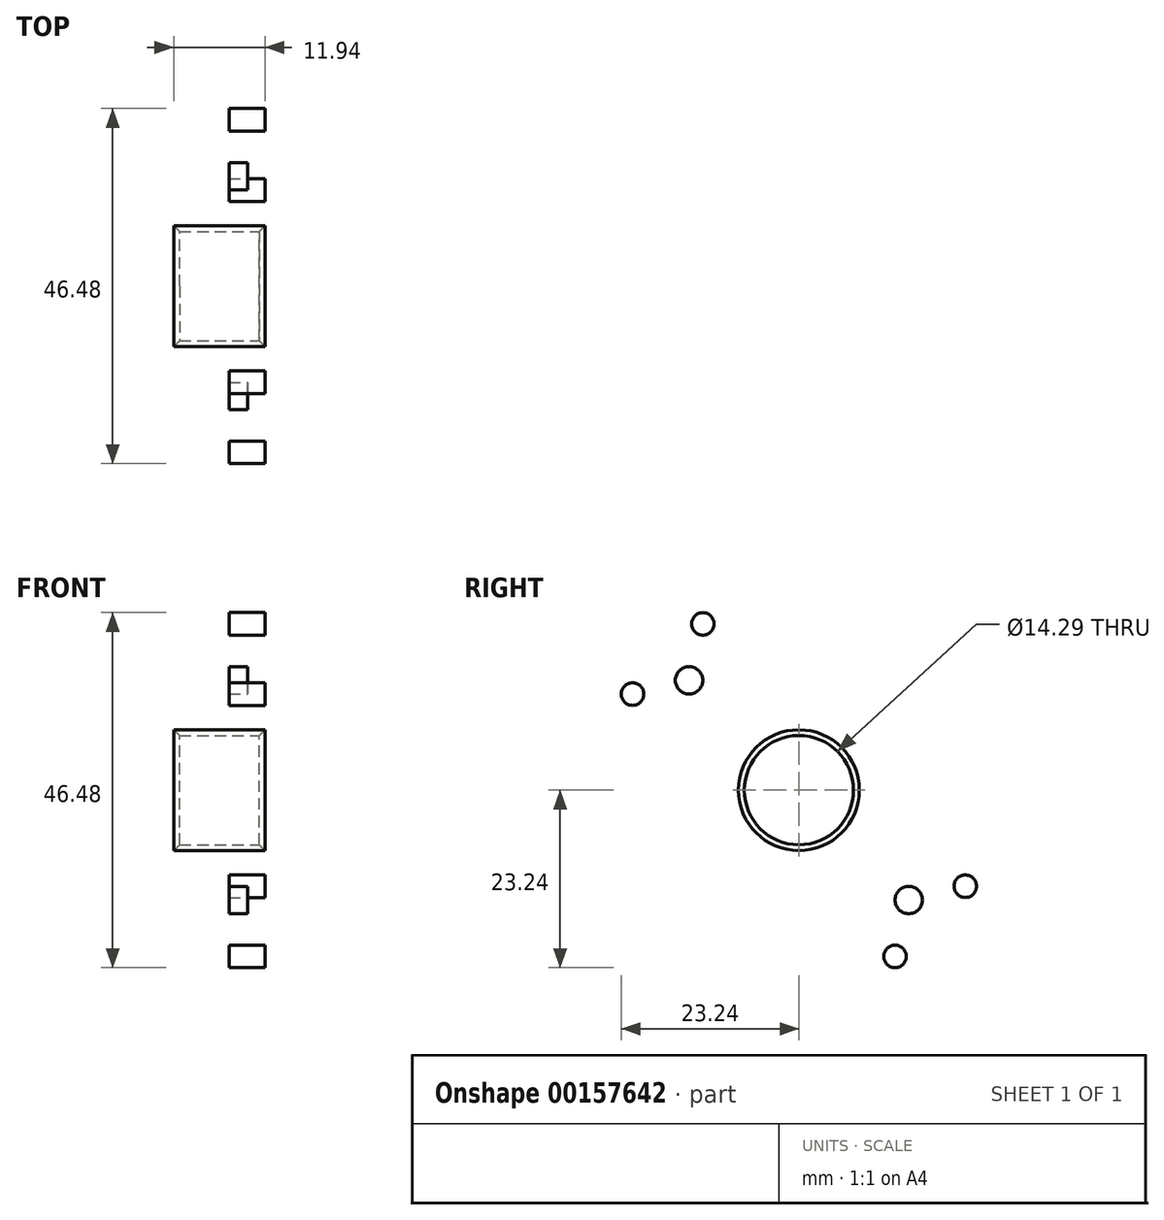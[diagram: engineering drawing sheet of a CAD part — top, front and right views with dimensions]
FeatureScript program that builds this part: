
annotation { "Feature Type Name" : "Feature", "Feature Type Description" : "" }
export const myFeature = defineFeature(function(context is Context, id is Id, definition is map)
    precondition{}
    {
        {
            var Q0;
            Q0=qCreatedBy(makeId("Right.planeOp"),FACE);
            var sketch = newSketch(context, id + "F0", { "sketchPlane" : qUnion([Q0])});
            skCircle(sketch, "E0", {"center": v(0, 0) * mm, "radius": 7.14 * mm});
            skCircle(sketch, "E1", {"center": v(0, 0) * mm, "radius": 11.94 * mm});
            skCircle(sketch, "E2", {"center": v(0, 0) * mm, "radius": 12.32 * mm});
            skCircle(sketch, "E3", {"center": v(0, 0) * mm, "radius": 17.02 * mm});
            skCircle(sketch, "E4", {"center": v(0, 0) * mm, "radius": 22.99 * mm});
            skCircle(sketch, "E5", {"center": v(0, 0) * mm, "radius": 27.3 * mm});
            skSolve(sketch);
        }
        {
            var Q0;
            Q0=makeQuery(id+"F0.imprint","IMPRINT",FACE,{"disambiguationData":[TD([[makeQuery(id+"F0.imprint","IMPRINT",EDGE,{"derivedFrom":sQuery(id+"F0.wireOp",EDGE,"E1")}),-1.0]])]});
            var Q1;
            Q1=makeQuery(id+"F0.imprint","IMPRINT",FACE,{"disambiguationData":[TD([[makeQuery(id+"F0.imprint","IMPRINT",EDGE,{"derivedFrom":sQuery(id+"F0.wireOp",EDGE,"E0")}),-1.0]])]});
            extrude(context, id + "F1", {"entities" : qUnion([Q0, Q1]), "oppositeDirection" : true, "depth" : 11.94 * mm});
        }
        {
            var Q0;
            Q0=makeQuery(id+"F0.imprint","IMPRINT",FACE,{"disambiguationData":[TD([[makeQuery(id+"F0.imprint","IMPRINT",EDGE,{"derivedFrom":sQuery(id+"F0.wireOp",EDGE,"E2")}),-1.0]])]});
            extrude(context, id + "F2", {"entities" : qUnion([Q0]), "operationType" : NewBodyOperationType.ADD, "oppositeDirection" : true, "depth" : 7.62 * mm});
        }
        {
            var Q0;
            Q0=makeQuery(id+"F0.imprint","IMPRINT",FACE,{"disambiguationData":[TD([[makeQuery(id+"F0.imprint","IMPRINT",EDGE,{"derivedFrom":sQuery(id+"F0.wireOp",EDGE,"E4")}),-1.0]])]});
            var Q1;
            Q1=makeQuery(id+"F0.imprint","IMPRINT",FACE,{"disambiguationData":[TD([[makeQuery(id+"F0.imprint","IMPRINT",EDGE,{"derivedFrom":sQuery(id+"F0.wireOp",EDGE,"E3")}),-1.0]])]});
            extrude(context, id + "F3", {"entities" : qUnion([Q0, Q1]), "operationType" : NewBodyOperationType.ADD, "oppositeDirection" : true, "depth" : 4.7 * mm});
        }
        {
            var Q0;
            Q0=makeQuery(id+"F1.opExtrude","CAP_EDGE",EDGE,{"disambiguationData":[OSD([sQuery(id+"F0.wireOp",EDGE,"E2")])],"isStart":false});
            chamfer(context, id + "F4", {"entities" : qUnion([Q0]), "width" : 1.52 * mm, "tangentPropagation" : true});
        }
        {
            var Q0;
            Q0=makeQuery(id+"F1.opExtrude","CAP_EDGE",EDGE,{"disambiguationData":[OSD([sQuery(id+"F0.wireOp",EDGE,"E0")])],"isStart":false});
            var Q1;
            Q1=makeQuery(id+"F1.opExtrude","CAP_EDGE",EDGE,{"disambiguationData":[OSD([sQuery(id+"F0.wireOp",EDGE,"E0")])],"isStart":true});
            chamfer(context, id + "F5", {"entities" : qUnion([Q0, Q1]), "width" : 0.76 * mm, "tangentPropagation" : true});
        }
        {
            var Q0;
            {var subQ0=sQuery(id+"F0.wireOp",EDGE,"E3");var subQ1=sQuery(id+"F0.wireOp",EDGE,"E2");Q0=makeQuery(id+"F3.boolean.opBoolean","MERGE",FACE,{"derivedFrom":[makeQuery(id+"F2.boolean.opBoolean","MERGE",FACE,{"derivedFrom":[makeQuery(id+"F1.opExtrude","CAP_FACE",FACE,{"disambiguationData":[OSD([sQuery(id+"F0.wireOp",EDGE,"E0"),subQ1])],"isStart":true}),makeQuery(id+"F2.opExtrude","CAP_FACE",FACE,{"disambiguationData":[OSD([subQ1,subQ0])],"isStart":true})]}),makeQuery(id+"F3.opExtrude","CAP_FACE",FACE,{"disambiguationData":[OSD([subQ0,sQuery(id+"F0.wireOp",EDGE,"E5")])],"isStart":true})]});}
            var sketch = newSketch(context, id + "F6", { "sketchPlane" : qUnion([Q0])});
            skCircle(sketch, "E6", {"center": v(12.57, 21.77) * mm, "radius": 1.47 * mm});
            skCircle(sketch, "E7", {"center": v(21.77, 12.57) * mm, "radius": 1.47 * mm});
            skCircle(sketch, "E8.MirrorC", {"center": v(-12.57, 21.77) * mm, "radius": 1.47 * mm});
            skCircle(sketch, "E9.MirrorC", {"center": v(-21.77, 12.57) * mm, "radius": 1.47 * mm});
            skCircle(sketch, "E10.MirrorC", {"center": v(-21.77, -12.57) * mm, "radius": 1.47 * mm});
            skCircle(sketch, "E11.MirrorC", {"center": v(-12.57, -21.77) * mm, "radius": 1.47 * mm});
            skCircle(sketch, "E12.MirrorC", {"center": v(12.57, -21.77) * mm, "radius": 1.47 * mm});
            skCircle(sketch, "E13.MirrorC", {"center": v(21.77, -12.57) * mm, "radius": 1.47 * mm});
            skCircle(sketch, "E14", {"center": v(14.38, 14.38) * mm, "radius": 1.8 * mm});
            skCircle(sketch, "E15.MirrorC", {"center": v(-14.38, 14.38) * mm, "radius": 1.8 * mm});
            skCircle(sketch, "E16.MirrorC", {"center": v(-14.38, -14.38) * mm, "radius": 1.8 * mm});
            skCircle(sketch, "E17.MirrorC", {"center": v(14.38, -14.38) * mm, "radius": 1.8 * mm});
            skSolve(sketch);
        }
        {
            var Q0;
            Q0=makeQuery(id+"F6.imprint","IMPRINT",FACE,{"disambiguationData":[TD([[makeQuery(id+"F6.imprint","IMPRINT",EDGE,{"derivedFrom":sQuery(id+"F6.wireOp",EDGE,"E8.MirrorC")}),-1.0]])]});
            var Q1;
            Q1=makeQuery(id+"F6.imprint","IMPRINT",FACE,{"disambiguationData":[TD([[makeQuery(id+"F6.imprint","IMPRINT",EDGE,{"derivedFrom":sQuery(id+"F6.wireOp",EDGE,"E9.MirrorC")}),-1.0]])]});
            var Q2;
            Q2=makeQuery(id+"F6.imprint","IMPRINT",FACE,{"disambiguationData":[TD([[makeQuery(id+"F6.imprint","IMPRINT",EDGE,{"derivedFrom":sQuery(id+"F6.wireOp",EDGE,"E10.MirrorC")}),1.0]])]});
            var Q3;
            Q3=makeQuery(id+"F6.imprint","IMPRINT",FACE,{"disambiguationData":[TD([[makeQuery(id+"F6.imprint","IMPRINT",EDGE,{"derivedFrom":sQuery(id+"F6.wireOp",EDGE,"E6")}),1.0]])]});
            var Q4;
            Q4=makeQuery(id+"F6.imprint","IMPRINT",FACE,{"disambiguationData":[TD([[makeQuery(id+"F6.imprint","IMPRINT",EDGE,{"derivedFrom":sQuery(id+"F6.wireOp",EDGE,"E7")}),1.0]])]});
            var Q5;
            Q5=makeQuery(id+"F6.imprint","IMPRINT",FACE,{"disambiguationData":[TD([[makeQuery(id+"F6.imprint","IMPRINT",EDGE,{"derivedFrom":sQuery(id+"F6.wireOp",EDGE,"E13.MirrorC")}),-1.0]])]});
            var Q6;
            Q6=makeQuery(id+"F6.imprint","IMPRINT",FACE,{"disambiguationData":[TD([[makeQuery(id+"F6.imprint","IMPRINT",EDGE,{"derivedFrom":sQuery(id+"F6.wireOp",EDGE,"E12.MirrorC")}),-1.0]])]});
            var Q7;
            Q7=makeQuery(id+"F6.imprint","IMPRINT",FACE,{"disambiguationData":[TD([[makeQuery(id+"F6.imprint","IMPRINT",EDGE,{"derivedFrom":sQuery(id+"F6.wireOp",EDGE,"E11.MirrorC")}),1.0]])]});
            var Q8;
            Q8=makeQuery(id+"F6.imprint","IMPRINT",FACE,{"disambiguationData":[TD([[makeQuery(id+"F6.imprint","IMPRINT",EDGE,{"derivedFrom":sQuery(id+"F6.wireOp",EDGE,"E15.MirrorC")}),-1.0]])]});
            var Q9;
            Q9=makeQuery(id+"F6.imprint","IMPRINT",FACE,{"disambiguationData":[TD([[makeQuery(id+"F6.imprint","IMPRINT",EDGE,{"derivedFrom":sQuery(id+"F6.wireOp",EDGE,"E14")}),1.0]])]});
            var Q10;
            Q10=makeQuery(id+"F6.imprint","IMPRINT",FACE,{"disambiguationData":[TD([[makeQuery(id+"F6.imprint","IMPRINT",EDGE,{"derivedFrom":sQuery(id+"F6.wireOp",EDGE,"E17.MirrorC")}),-1.0]])]});
            var Q11;
            Q11=makeQuery(id+"F6.imprint","IMPRINT",FACE,{"disambiguationData":[TD([[makeQuery(id+"F6.imprint","IMPRINT",EDGE,{"derivedFrom":sQuery(id+"F6.wireOp",EDGE,"E16.MirrorC")}),1.0]])]});
            extrude(context, id + "F7", {"entities" : qUnion([Q0, Q1, Q2, Q3, Q4, Q5, Q6, Q7, Q8, Q9, Q10, Q11]), "operationType" : NewBodyOperationType.REMOVE, "oppositeDirection" : true, "depth" : 25.4 * mm});
        }
        {
            var Q0;
            Q0=makeQuery(id+"F0.imprint","IMPRINT",FACE,{"disambiguationData":[TD([[makeQuery(id+"F0.imprint","IMPRINT",EDGE,{"derivedFrom":sQuery(id+"F0.wireOp",EDGE,"E3")}),-1.0]])]});
            var Q1;
            Q1=makeQuery(id+"F0.imprint","IMPRINT",FACE,{"disambiguationData":[TD([[makeQuery(id+"F0.imprint","IMPRINT",EDGE,{"derivedFrom":sQuery(id+"F0.wireOp",EDGE,"E2")}),-1.0]])]});
            var Q2;
            Q2=makeQuery(id+"F0.imprint","IMPRINT",FACE,{"disambiguationData":[TD([[makeQuery(id+"F0.imprint","IMPRINT",EDGE,{"derivedFrom":sQuery(id+"F0.wireOp",EDGE,"E1")}),-1.0]])]});
            extrude(context, id + "F8", {"entities" : qUnion([Q0, Q1, Q2]), "operationType" : NewBodyOperationType.REMOVE, "oppositeDirection" : true, "depth" : 2.3 * mm});
        }
        {
            var Q0;
            {var subQ0=sQuery(id+"F0.wireOp",EDGE,"E0");var subQ1=sQuery(id+"F0.wireOp",EDGE,"E3");var subQ2=sQuery(id+"F0.wireOp",EDGE,"E2");Q0=makeQuery(id+"F8.boolean.opBoolean","SPLIT",FACE,{"disambiguationData":[TD([makeQuery(id+"F8.opExtrude","SWEPT_FACE",FACE,{"disambiguationData":[OSD([sQuery(id+"F0.wireOp",EDGE,"E1")])]})])],"derivedFrom":makeQuery(id+"F3.boolean.opBoolean","MERGE",FACE,{"derivedFrom":[makeQuery(id+"F2.boolean.opBoolean","MERGE",FACE,{"derivedFrom":[makeQuery(id+"F1.opExtrude","CAP_FACE",FACE,{"disambiguationData":[OSD([subQ0,subQ2])],"isStart":true}),makeQuery(id+"F2.opExtrude","CAP_FACE",FACE,{"disambiguationData":[OSD([subQ2,subQ1])],"isStart":true})]}),makeQuery(id+"F3.opExtrude","CAP_FACE",FACE,{"disambiguationData":[OSD([subQ1,sQuery(id+"F0.wireOp",EDGE,"E5")])],"isStart":true})]})});}
            var sketch = newSketch(context, id + "F9", { "sketchPlane" : qUnion([Q0])});
            skCircle(sketch, "E18", {"center": v(0, 9.4) * mm, "radius": 1.1 * mm});
            skCircle(sketch, "E19", {"center": v(8.13, 4.7) * mm, "radius": 1.1 * mm});
            skCircle(sketch, "E20.MirrorC", {"center": v(-8.13, 4.7) * mm, "radius": 1.1 * mm});
            skCircle(sketch, "E21.MirrorC", {"center": v(-8.13, -4.7) * mm, "radius": 1.1 * mm});
            skCircle(sketch, "E22.MirrorC", {"center": v(0, -9.4) * mm, "radius": 1.1 * mm});
            skCircle(sketch, "E23.MirrorC", {"center": v(8.13, -4.7) * mm, "radius": 1.1 * mm});
            skSolve(sketch);
        }
        {
            var Q0;
            Q0=makeQuery(id+"F9.imprint","IMPRINT",FACE,{"disambiguationData":[TD([[makeQuery(id+"F9.imprint","IMPRINT",EDGE,{"derivedFrom":sQuery(id+"F9.wireOp",EDGE,"E20.MirrorC")}),-1.0]])]});
            var Q1;
            Q1=makeQuery(id+"F9.imprint","IMPRINT",FACE,{"disambiguationData":[TD([[makeQuery(id+"F9.imprint","IMPRINT",EDGE,{"derivedFrom":sQuery(id+"F9.wireOp",EDGE,"E18")}),1.0]])]});
            var Q2;
            Q2=makeQuery(id+"F9.imprint","IMPRINT",FACE,{"disambiguationData":[TD([[makeQuery(id+"F9.imprint","IMPRINT",EDGE,{"derivedFrom":sQuery(id+"F9.wireOp",EDGE,"E19")}),1.0]])]});
            var Q3;
            Q3=makeQuery(id+"F9.imprint","IMPRINT",FACE,{"disambiguationData":[TD([[makeQuery(id+"F9.imprint","IMPRINT",EDGE,{"derivedFrom":sQuery(id+"F9.wireOp",EDGE,"E23.MirrorC")}),-1.0]])]});
            var Q4;
            Q4=makeQuery(id+"F9.imprint","IMPRINT",FACE,{"disambiguationData":[TD([[makeQuery(id+"F9.imprint","IMPRINT",EDGE,{"derivedFrom":sQuery(id+"F9.wireOp",EDGE,"E22.MirrorC")}),-1.0]])]});
            var Q5;
            Q5=makeQuery(id+"F9.imprint","IMPRINT",FACE,{"disambiguationData":[TD([[makeQuery(id+"F9.imprint","IMPRINT",EDGE,{"derivedFrom":sQuery(id+"F9.wireOp",EDGE,"E21.MirrorC")}),1.0]])]});
            extrude(context, id + "F10", {"entities" : qUnion([Q0, Q1, Q2, Q3, Q4, Q5]), "operationType" : NewBodyOperationType.REMOVE, "oppositeDirection" : true, "depth" : 9.65 * mm});
        }
    });
